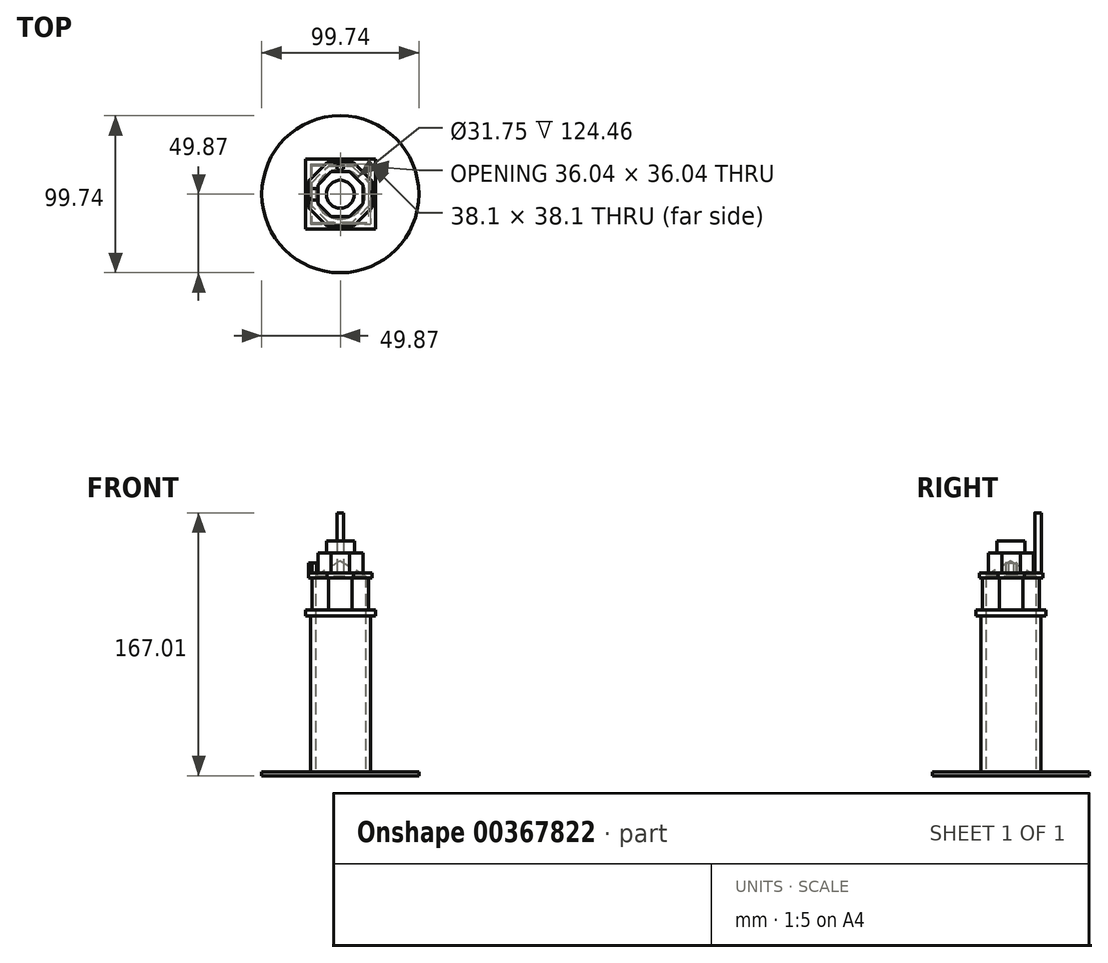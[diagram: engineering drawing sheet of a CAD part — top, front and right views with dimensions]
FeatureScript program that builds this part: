
annotation { "Feature Type Name" : "Feature", "Feature Type Description" : "" }
export const myFeature = defineFeature(function(context is Context, id is Id, definition is map)
    precondition{}
    {
        {
            var Q0;
            Q0=qCreatedBy(makeId("Top.planeOp"),FACE);
            var sketch = newSketch(context, id + "F0", { "sketchPlane" : qUnion([Q0])});
            skLineSegment(sketch, "E0.bottom", {"start": v(-19.05, 19.05) * mm, "end": v(19.05, 19.05) * mm});
            skLineSegment(sketch, "E0.top", {"start": v(-19.05, -19.05) * mm, "end": v(19.05, -19.05) * mm});
            skLineSegment(sketch, "E0.left", {"start": v(-19.05, 19.05) * mm, "end": v(-19.05, -19.05) * mm});
            skLineSegment(sketch, "E0.right", {"start": v(19.05, 19.05) * mm, "end": v(19.05, -19.05) * mm});
            skPoint(sketch, "E0.middle", {"position": v(0, 0) * mm});
            skSolve(sketch);
        }
        {
            var Q0;
            Q0 = qSketchRegion(id + "F0", true);
            extrude(context, id + "F1", {"entities" : qUnion([Q0]), "depth" : 101.6 * mm});
        }
        {
            var Q0;
            Q0=makeQuery(id+"F1.opExtrude","CAP_FACE",FACE,{"disambiguationData":[OSD([sQuery(id+"F0.wireOp",EDGE,"E0.bottom"),sQuery(id+"F0.wireOp",EDGE,"E0.top"),sQuery(id+"F0.wireOp",EDGE,"E0.left"),sQuery(id+"F0.wireOp",EDGE,"E0.right")])],"isStart":false});
            var sketch = newSketch(context, id + "F2", { "sketchPlane" : qUnion([Q0])});
            skLineSegment(sketch, "E1.bottom", {"start": v(-22.22, 22.23) * mm, "end": v(22.23, 22.23) * mm});
            skLineSegment(sketch, "E1.top", {"start": v(-22.23, -22.23) * mm, "end": v(22.22, -22.23) * mm});
            skLineSegment(sketch, "E1.left", {"start": v(-22.22, 22.23) * mm, "end": v(-22.23, -22.23) * mm});
            skLineSegment(sketch, "E1.right", {"start": v(22.23, 22.23) * mm, "end": v(22.22, -22.23) * mm});
            skPoint(sketch, "E1.middle", {"position": v(0, 0) * mm});
            skSolve(sketch);
        }
        {
            var Q0;
            Q0 = qSketchRegion(id + "F2", true);
            extrude(context, id + "F3", {"entities" : qUnion([Q0]), "operationType" : NewBodyOperationType.ADD, "depth" : 3.8 * mm});
        }
        {
            var Q0;
            Q0=makeQuery(id+"F3.opExtrude","CAP_FACE",FACE,{"disambiguationData":[OSD([sQuery(id+"F2.wireOp",EDGE,"E1.bottom"),sQuery(id+"F2.wireOp",EDGE,"E1.top"),sQuery(id+"F2.wireOp",EDGE,"E1.left"),sQuery(id+"F2.wireOp",EDGE,"E1.right")])],"isStart":false});
            var sketch = newSketch(context, id + "F4", { "sketchPlane" : qUnion([Q0])});
            skCircle(sketch, "E2.cCircle", {"center": v(0, 0) * mm, "radius": 18.02 * mm, "construction": true});
            skPoint(sketch, "E2.cCircle.perimeterSnap0", {"position": v(0, 22.23) * mm});
            skLineSegment(sketch, "E2.0", {"start": v(-7.46, 18.02) * mm, "end": v(7.46, 18.02) * mm});
            skLineSegment(sketch, "E2.1", {"start": v(7.46, 18.02) * mm, "end": v(18.02, 7.46) * mm});
            skLineSegment(sketch, "E2.2", {"start": v(18.02, 7.46) * mm, "end": v(18.02, -7.46) * mm});
            skLineSegment(sketch, "E2.3", {"start": v(18.02, -7.46) * mm, "end": v(7.46, -18.02) * mm});
            skLineSegment(sketch, "E2.4", {"start": v(7.46, -18.02) * mm, "end": v(-7.46, -18.02) * mm});
            skLineSegment(sketch, "E2.5", {"start": v(-7.46, -18.02) * mm, "end": v(-18.02, -7.46) * mm});
            skLineSegment(sketch, "E2.6", {"start": v(-18.02, -7.46) * mm, "end": v(-18.02, 7.46) * mm});
            skLineSegment(sketch, "E2.7", {"start": v(-18.02, 7.46) * mm, "end": v(-7.46, 18.02) * mm});
            skPoint(sketch, "E2.0.midPoint", {"position": v(0, 18.02) * mm});
            skPoint(sketch, "E2.0.midPoint.positionSnap0", {"position": v(0, 22.23) * mm});
            skSolve(sketch);
        }
        {
            var Q0;
            Q0 = qSketchRegion(id + "F4", true);
            extrude(context, id + "F5", {"entities" : qUnion([Q0]), "operationType" : NewBodyOperationType.ADD, "depth" : 20.32 * mm});
        }
        {
            var Q0;
            Q0=makeQuery(id+"F5.opExtrude","CAP_FACE",FACE,{"disambiguationData":[OSD([sQuery(id+"F4.wireOp",EDGE,"E2.0"),sQuery(id+"F4.wireOp",EDGE,"E2.1"),sQuery(id+"F4.wireOp",EDGE,"E2.2"),sQuery(id+"F4.wireOp",EDGE,"E2.3"),sQuery(id+"F4.wireOp",EDGE,"E2.4"),sQuery(id+"F4.wireOp",EDGE,"E2.5"),sQuery(id+"F4.wireOp",EDGE,"E2.6"),sQuery(id+"F4.wireOp",EDGE,"E2.7")])],"isStart":false});
            var sketch = newSketch(context, id + "F6", { "sketchPlane" : qUnion([Q0])});
            skCircle(sketch, "E3.cCircle", {"center": v(0, 0) * mm, "radius": 20.22 * mm, "construction": true});
            skPoint(sketch, "E3.cCircle.perimeterSnap0", {"position": v(0, 18.02) * mm});
            skLineSegment(sketch, "E3.0", {"start": v(-8.38, 20.22) * mm, "end": v(8.38, 20.22) * mm});
            skLineSegment(sketch, "E3.1", {"start": v(8.38, 20.22) * mm, "end": v(20.22, 8.38) * mm});
            skLineSegment(sketch, "E3.2", {"start": v(20.22, 8.38) * mm, "end": v(20.22, -8.38) * mm});
            skLineSegment(sketch, "E3.3", {"start": v(20.22, -8.38) * mm, "end": v(8.38, -20.22) * mm});
            skLineSegment(sketch, "E3.4", {"start": v(8.38, -20.22) * mm, "end": v(-8.38, -20.22) * mm});
            skLineSegment(sketch, "E3.5", {"start": v(-8.38, -20.22) * mm, "end": v(-20.22, -8.38) * mm});
            skLineSegment(sketch, "E3.6", {"start": v(-20.22, -8.38) * mm, "end": v(-20.22, 8.38) * mm});
            skLineSegment(sketch, "E3.7", {"start": v(-20.22, 8.38) * mm, "end": v(-8.38, 20.22) * mm});
            skPoint(sketch, "E3.0.midPoint", {"position": v(0, 20.22) * mm});
            skPoint(sketch, "E3.0.midPoint.positionSnap0", {"position": v(0, 18.02) * mm});
            skSolve(sketch);
        }
        {
            var Q0;
            Q0 = qSketchRegion(id + "F6", true);
            extrude(context, id + "F7", {"entities" : qUnion([Q0]), "operationType" : NewBodyOperationType.ADD, "depth" : 3.17 * mm});
        }
        {
            var Q0;
            Q0=makeQuery(id+"F7.opExtrude","CAP_FACE",FACE,{"disambiguationData":[OSD([sQuery(id+"F6.wireOp",EDGE,"E3.0"),sQuery(id+"F6.wireOp",EDGE,"E3.1"),sQuery(id+"F6.wireOp",EDGE,"E3.2"),sQuery(id+"F6.wireOp",EDGE,"E3.3"),sQuery(id+"F6.wireOp",EDGE,"E3.4"),sQuery(id+"F6.wireOp",EDGE,"E3.5"),sQuery(id+"F6.wireOp",EDGE,"E3.6"),sQuery(id+"F6.wireOp",EDGE,"E3.7")])],"isStart":false});
            var sketch = newSketch(context, id + "F8", { "sketchPlane" : qUnion([Q0])});
            skCircle(sketch, "E4.cCircle", {"center": v(0, 0) * mm, "radius": 14.3 * mm, "construction": true});
            skPoint(sketch, "E4.cCircle.perimeterSnap0", {"position": v(-14.3, 14.3) * mm});
            skLineSegment(sketch, "E4.0", {"start": v(-5.92, 14.3) * mm, "end": v(5.92, 14.3) * mm});
            skLineSegment(sketch, "E4.1", {"start": v(5.92, 14.3) * mm, "end": v(14.3, 5.92) * mm});
            skLineSegment(sketch, "E4.2", {"start": v(14.3, 5.92) * mm, "end": v(14.3, -5.92) * mm});
            skLineSegment(sketch, "E4.3", {"start": v(14.3, -5.92) * mm, "end": v(5.92, -14.3) * mm});
            skLineSegment(sketch, "E4.4", {"start": v(5.92, -14.3) * mm, "end": v(-5.92, -14.3) * mm});
            skLineSegment(sketch, "E4.5", {"start": v(-5.92, -14.3) * mm, "end": v(-14.3, -5.92) * mm});
            skLineSegment(sketch, "E4.6", {"start": v(-14.3, -5.92) * mm, "end": v(-14.3, 5.92) * mm});
            skLineSegment(sketch, "E4.7", {"start": v(-14.3, 5.92) * mm, "end": v(-5.92, 14.3) * mm});
            skPoint(sketch, "E4.0.midPoint", {"position": v(0, 14.3) * mm});
            skPoint(sketch, "E4.0.midPoint.positionSnap0", {"position": v(-14.3, 14.3) * mm});
            skSolve(sketch);
        }
        {
            var Q0;
            Q0 = qSketchRegion(id + "F8", true);
            extrude(context, id + "F9", {"entities" : qUnion([Q0]), "operationType" : NewBodyOperationType.ADD, "depth" : 12.7 * mm});
        }
        {
            var Q0;
            Q0=makeQuery(id+"F7.opExtrude","CAP_FACE",FACE,{"disambiguationData":[OSD([sQuery(id+"F6.wireOp",EDGE,"E3.0"),sQuery(id+"F6.wireOp",EDGE,"E3.1"),sQuery(id+"F6.wireOp",EDGE,"E3.2"),sQuery(id+"F6.wireOp",EDGE,"E3.3"),sQuery(id+"F6.wireOp",EDGE,"E3.4"),sQuery(id+"F6.wireOp",EDGE,"E3.5"),sQuery(id+"F6.wireOp",EDGE,"E3.6"),sQuery(id+"F6.wireOp",EDGE,"E3.7")])],"isStart":false});
            var sketch = newSketch(context, id + "F10", { "sketchPlane" : qUnion([Q0])});
            skCircle(sketch, "E5", {"center": v(0, 17.24) * mm, "radius": 2.1 * mm});
            skSolve(sketch);
        }
        {
            var Q0;
            Q0 = qSketchRegion(id + "F10", true);
            extrude(context, id + "F11", {"entities" : qUnion([Q0]), "operationType" : NewBodyOperationType.ADD, "depth" : 38.1 * mm});
        }
        {
            var Q0;
            Q0=makeQuery(id+"F7.opExtrude","CAP_FACE",FACE,{"disambiguationData":[OSD([sQuery(id+"F6.wireOp",EDGE,"E3.0"),sQuery(id+"F6.wireOp",EDGE,"E3.1"),sQuery(id+"F6.wireOp",EDGE,"E3.2"),sQuery(id+"F6.wireOp",EDGE,"E3.3"),sQuery(id+"F6.wireOp",EDGE,"E3.4"),sQuery(id+"F6.wireOp",EDGE,"E3.5"),sQuery(id+"F6.wireOp",EDGE,"E3.6"),sQuery(id+"F6.wireOp",EDGE,"E3.7")])],"isStart":false});
            var sketch = newSketch(context, id + "F12", { "sketchPlane" : qUnion([Q0])});
            skCircle(sketch, "E6.cCircle", {"center": v(-16.5, 0) * mm, "radius": 3.71 * mm, "construction": true});
            skPoint(sketch, "E6.cCircle.centerSnap0", {"position": v(-20.22, 0) * mm});
            skLineSegment(sketch, "E6.0", {"start": v(-20.22, -1.54) * mm, "end": v(-20.22, 1.54) * mm});
            skLineSegment(sketch, "E6.1", {"start": v(-20.22, 1.54) * mm, "end": v(-18.05, 3.71) * mm});
            skLineSegment(sketch, "E6.2", {"start": v(-18.05, 3.71) * mm, "end": v(-14.97, 3.71) * mm});
            skLineSegment(sketch, "E6.3", {"start": v(-14.97, 3.71) * mm, "end": v(-12.8, 1.54) * mm});
            skLineSegment(sketch, "E6.4", {"start": v(-12.8, 1.54) * mm, "end": v(-12.8, -1.54) * mm});
            skLineSegment(sketch, "E6.5", {"start": v(-12.8, -1.54) * mm, "end": v(-14.97, -3.71) * mm});
            skLineSegment(sketch, "E6.6", {"start": v(-14.97, -3.71) * mm, "end": v(-18.05, -3.71) * mm});
            skLineSegment(sketch, "E6.7", {"start": v(-18.05, -3.71) * mm, "end": v(-20.22, -1.54) * mm});
            skPoint(sketch, "E6.0.midPoint", {"position": v(-20.22, 0) * mm});
            skSolve(sketch);
        }
        {
            var Q0;
            Q0 = qSketchRegion(id + "F12", true);
            extrude(context, id + "F13", {"entities" : qUnion([Q0]), "operationType" : NewBodyOperationType.ADD, "depth" : 6.35 * mm});
        }
        {
            var Q0;
            Q0=makeQuery(id+"F11.opExtrude","CAP_FACE",FACE,{"disambiguationData":[OSD([sQuery(id+"F10.wireOp",EDGE,"E5")])],"isStart":false});
            var sketch = newSketch(context, id + "F14", { "sketchPlane" : qUnion([Q0])});
            skSolve(sketch);
        }
        {
            var Q0;
            Q0=makeQuery(id+"F1.opExtrude","CAP_FACE",FACE,{"disambiguationData":[OSD([sQuery(id+"F0.wireOp",EDGE,"E0.bottom"),sQuery(id+"F0.wireOp",EDGE,"E0.top"),sQuery(id+"F0.wireOp",EDGE,"E0.left"),sQuery(id+"F0.wireOp",EDGE,"E0.right")])],"isStart":true});
            var sketch = newSketch(context, id + "F15", { "sketchPlane" : qUnion([Q0])});
            skPoint(sketch, "E7", {"position": v(0, 0) * mm});
            skSolve(sketch);
        }
        {
            var Q0;
            Q0=sQuery(id+"F15.wireOp",VERTEX,"E7");
            var Q1;
            Q1=makeQuery(id+"F1.opExtrude","SWEPT_BODY",BODY,{"disambiguationData":[OSD([sQuery(id+"F0.wireOp",EDGE,"E0.bottom"),sQuery(id+"F0.wireOp",EDGE,"E0.top"),sQuery(id+"F0.wireOp",EDGE,"E0.left"),sQuery(id+"F0.wireOp",EDGE,"E0.right")])]});
            hole(context, id + "F16", {"style" : HoleStyle.SIMPLE, "endStyle" : HoleEndStyle.BLIND, "holeDiameter" : 31.75 * mm, "holeDepth" : 127 * mm, "isTappedThrough" : true, "tappedDepth" : 12.7 * mm, "tapClearance" : 3, "locations" : qUnion([Q0]), "scope" : qUnion([Q1])});
        }
        {
            var Q0;
            Q0=makeQuery(id+"F9.opExtrude","CAP_FACE",FACE,{"disambiguationData":[OSD([sQuery(id+"F8.wireOp",EDGE,"E4.0"),sQuery(id+"F8.wireOp",EDGE,"E4.1"),sQuery(id+"F8.wireOp",EDGE,"E4.2"),sQuery(id+"F8.wireOp",EDGE,"E4.3"),sQuery(id+"F8.wireOp",EDGE,"E4.4"),sQuery(id+"F8.wireOp",EDGE,"E4.5"),sQuery(id+"F8.wireOp",EDGE,"E4.6"),sQuery(id+"F8.wireOp",EDGE,"E4.7")])],"isStart":false});
            var sketch = newSketch(context, id + "F17", { "sketchPlane" : qUnion([Q0])});
            skPoint(sketch, "E8", {"position": v(0, 0) * mm});
            skSolve(sketch);
        }
        {
            var Q0;
            Q0=makeQuery(id+"F17.imprint","IMPRINT",FACE,{"disambiguationData":[TD([[makeQuery(id+"F17.imprint","IMPRINT",EDGE,{"derivedFrom":makeQuery(id+"F9.opExtrude","CAP_EDGE",EDGE,{"disambiguationData":[OSD([sQuery(id+"F8.wireOp",EDGE,"E4.0")])],"isStart":false})}),-1.0]])]});
            var sketch = newSketch(context, id + "F18", { "sketchPlane" : qUnion([Q0])});
            skSolve(sketch);
        }
        {
            var Q0;
            Q0=qCreatedBy(makeId("Top.planeOp"),FACE);
            var sketch = newSketch(context, id + "F19", { "sketchPlane" : qUnion([Q0])});
            skCircle(sketch, "E9", {"center": v(0, 0) * mm, "radius": 49.87 * mm});
            skSolve(sketch);
        }
        {
            var Q0;
            Q0 = qSketchRegion(id + "F19", true);
            extrude(context, id + "F20", {"entities" : qUnion([Q0]), "operationType" : NewBodyOperationType.ADD, "depth" : 2.54 * mm});
        }
        {
            var Q0;
            Q0=makeQuery(id+"F18.imprint","IMPRINT",FACE,{"disambiguationData":[TD([[makeQuery(id+"F18.imprint","IMPRINT",EDGE,{"derivedFrom":makeQuery(id+"F17.imprint","IMPRINT",EDGE,{"derivedFrom":makeQuery(id+"F9.opExtrude","CAP_EDGE",EDGE,{"disambiguationData":[OSD([sQuery(id+"F8.wireOp",EDGE,"E4.0")])],"isStart":false})})}),-1.0]])]});
            var sketch = newSketch(context, id + "F21", { "sketchPlane" : qUnion([Q0])});
            skCircle(sketch, "E10", {"center": v(0, 0) * mm, "radius": 8.9 * mm});
            skSolve(sketch);
        }
        {
            var Q0;
            Q0 = qSketchRegion(id + "F21", true);
            extrude(context, id + "F22", {"entities" : qUnion([Q0]), "operationType" : NewBodyOperationType.ADD, "depth" : 7.62 * mm});
        }
        {
            var Q0;
            Q0=makeQuery(id+"F22.opExtrude","CAP_FACE",FACE,{"disambiguationData":[OSD([sQuery(id+"F21.wireOp",EDGE,"E10")])],"isStart":false});
            var sketch = newSketch(context, id + "F23", { "sketchPlane" : qUnion([Q0])});
            skArc(sketch, "E11", {"start": v(-8.9, 0) * mm, "mid": v(0, 8.9) * mm, "end": v(8.9, 0) * mm});
            skLineSegment(sketch, "E12", {"start": v(-8.9, 0) * mm, "end": v(8.9, 0) * mm});
            skSolve(sketch);
        }
        {
            var Q0;
            Q0=sQuery(id+"F23.wireOp",EDGE,"E11");
            var Q1;
            Q1=sQuery(id+"F23.wireOp",EDGE,"E12");
            revolve(context, id + "F24", {"bodyType" : ToolBodyType.SURFACE, "surfaceEntities" : qUnion([Q0]), "axis" : qUnion([Q1]), "revolveType" : RevolveType.FULL});
        }
    });
